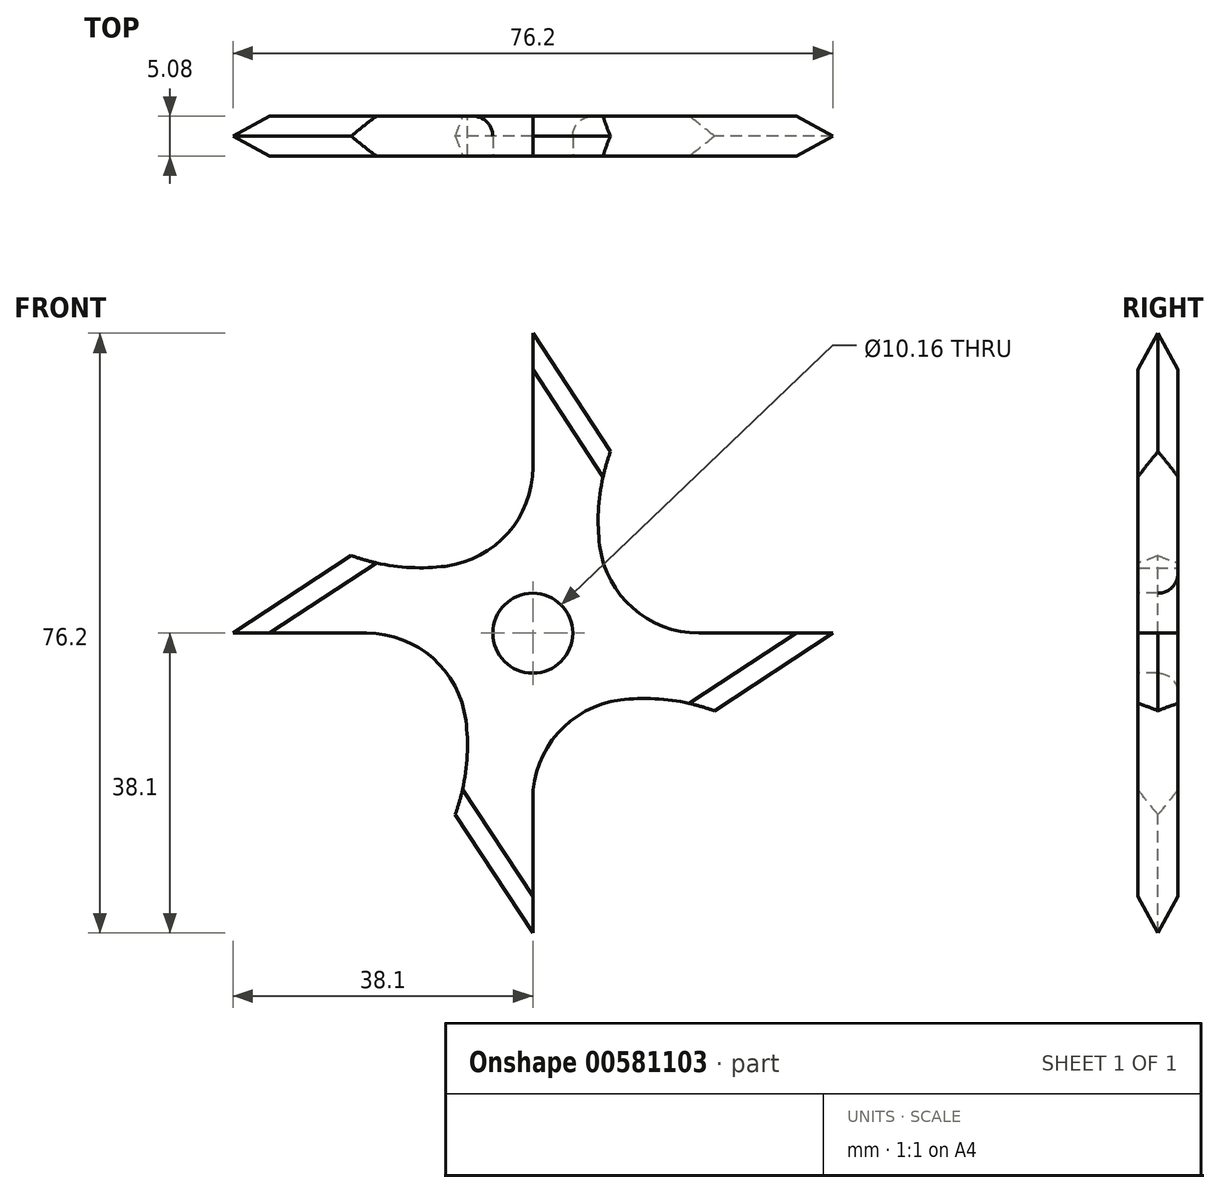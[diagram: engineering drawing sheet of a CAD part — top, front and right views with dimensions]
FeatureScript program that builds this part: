
annotation { "Feature Type Name" : "Feature", "Feature Type Description" : "" }
export const myFeature = defineFeature(function(context is Context, id is Id, definition is map)
    precondition{}
    {
        {
            var Q0;
            Q0=qCreatedBy(makeId("Front.planeOp"),FACE);
            var sketch = newSketch(context, id + "F0", { "sketchPlane" : qUnion([Q0])});
            skLineSegment(sketch, "E0", {"start": v(0, 0) * mm, "end": v(0, 38.1) * mm});
            skLineSegment(sketch, "E1", {"start": v(0, 0) * mm, "end": v(12.7, 0) * mm});
            skLineSegment(sketch, "E2", {"start": v(9.86, 23.06) * mm, "end": v(0, 38.1) * mm});
            skArc(sketch, "E3", {"start": v(9.86, 23.06) * mm, "mid": v(8.5, 11.19) * mm, "end": v(12.7, 0) * mm});
            skLineSegment(sketch, "E4.1.0", {"start": v(-23.06, 9.86) * mm, "end": v(-38.1, 0) * mm});
            skLineSegment(sketch, "E4.1.1", {"start": v(0, 0) * mm, "end": v(-38.1, 0) * mm});
            skArc(sketch, "E4.1.2", {"start": v(-23.06, 9.86) * mm, "mid": v(-11.19, 8.5) * mm, "end": v(0, 12.7) * mm});
            skLineSegment(sketch, "E4.1.3", {"start": v(0, 0) * mm, "end": v(0, 12.7) * mm});
            skLineSegment(sketch, "E4.2.0", {"start": v(-9.86, -23.06) * mm, "end": v(0, -38.1) * mm});
            skLineSegment(sketch, "E4.2.1", {"start": v(0, 0) * mm, "end": v(0, -38.1) * mm});
            skArc(sketch, "E4.2.2", {"start": v(-9.86, -23.06) * mm, "mid": v(-8.5, -11.19) * mm, "end": v(-12.7, 0) * mm});
            skLineSegment(sketch, "E4.2.3", {"start": v(0, 0) * mm, "end": v(-12.7, 0) * mm});
            skLineSegment(sketch, "E4.3.0", {"start": v(23.06, -9.86) * mm, "end": v(38.1, 0) * mm});
            skLineSegment(sketch, "E4.3.1", {"start": v(0, 0) * mm, "end": v(38.1, 0) * mm});
            skArc(sketch, "E4.3.2", {"start": v(23.06, -9.86) * mm, "mid": v(11.19, -8.5) * mm, "end": v(0, -12.7) * mm});
            skLineSegment(sketch, "E4.3.3", {"start": v(0, 0) * mm, "end": v(0, -12.7) * mm});
            skPoint(sketch, "E4.center", {"position": v(0, 0) * mm});
            skSolve(sketch);
        }
        {
            var Q0;
            Q0 = qSketchRegion(id + "F0", true);
            extrude(context, id + "F1", {"entities" : qUnion([Q0]), "depth" : 5.08 * mm, "offsetDistance" : 25.4 * mm});
        }
        {
            var Q0;
            Q0=makeQuery(id+"F1.opExtrude","CAP_FACE",FACE,{"disambiguationData":[OSD([sQuery(id+"F0.wireOp",EDGE,"E0"),sQuery(id+"F0.wireOp",EDGE,"E2"),sQuery(id+"F0.wireOp",EDGE,"E3"),sQuery(id+"F0.wireOp",EDGE,"E4.1.0"),sQuery(id+"F0.wireOp",EDGE,"E4.1.1"),sQuery(id+"F0.wireOp",EDGE,"E4.1.2"),sQuery(id+"F0.wireOp",EDGE,"E4.2.0"),sQuery(id+"F0.wireOp",EDGE,"E4.2.1"),sQuery(id+"F0.wireOp",EDGE,"E4.2.2"),sQuery(id+"F0.wireOp",EDGE,"E4.3.0"),sQuery(id+"F0.wireOp",EDGE,"E4.3.1"),sQuery(id+"F0.wireOp",EDGE,"E4.3.2")])],"isStart":false});
            var sketch = newSketch(context, id + "F2", { "sketchPlane" : qUnion([Q0])});
            skCircle(sketch, "E5", {"center": v(0, 0) * mm, "radius": 5.08 * mm});
            skSolve(sketch);
        }
        {
            var Q0;
            Q0 = qSketchRegion(id + "F2", true);
            extrude(context, id + "F3", {"entities" : qUnion([Q0]), "operationType" : NewBodyOperationType.REMOVE, "oppositeDirection" : true, "depth" : 25.4 * mm, "offsetDistance" : 25.4 * mm});
        }
        {
            var Q0;
            Q0=makeQuery(id+"F1.opExtrude","SWEPT_EDGE",EDGE,{"disambiguationData":[OSD([sQuery(id+"F0.wireOp",EDGE,"E0"),sQuery(id+"F0.wireOp",EDGE,"E4.1.2"),sQuery(id+"F0.wireOp",EDGE,"E4.1.3")])]});
            var Q1;
            Q1=makeQuery(id+"F1.opExtrude","SWEPT_EDGE",EDGE,{"disambiguationData":[OSD([sQuery(id+"F0.wireOp",EDGE,"E3"),sQuery(id+"F0.wireOp",EDGE,"E4.3.1")])]});
            var Q2;
            Q2=makeQuery(id+"F1.opExtrude","SWEPT_EDGE",EDGE,{"disambiguationData":[OSD([sQuery(id+"F0.wireOp",EDGE,"E4.2.1"),sQuery(id+"F0.wireOp",EDGE,"E4.3.2"),sQuery(id+"F0.wireOp",EDGE,"E4.3.3")])]});
            var Q3;
            Q3=makeQuery(id+"F1.opExtrude","SWEPT_EDGE",EDGE,{"disambiguationData":[OSD([sQuery(id+"F0.wireOp",EDGE,"E4.1.1"),sQuery(id+"F0.wireOp",EDGE,"E4.2.2"),sQuery(id+"F0.wireOp",EDGE,"E4.2.3")])]});
            fillet(context, id + "F4", {"entities" : qUnion([Q0, Q1, Q2, Q3]), "radius" : 12.7 * mm, "tangentPropagation" : true, "allowEdgeOverflow" : false});
        }
        {
            var Q0;
            Q0=makeQuery(id+"F1.opExtrude","CAP_EDGE",EDGE,{"disambiguationData":[OSD([sQuery(id+"F0.wireOp",EDGE,"E4.3.0")])],"isStart":true});
            var Q1;
            Q1=makeQuery(id+"F1.opExtrude","CAP_EDGE",EDGE,{"disambiguationData":[OSD([sQuery(id+"F0.wireOp",EDGE,"E4.3.0")])],"isStart":false});
            var Q2;
            Q2=makeQuery(id+"F1.opExtrude","CAP_EDGE",EDGE,{"disambiguationData":[OSD([sQuery(id+"F0.wireOp",EDGE,"E2")])],"isStart":true});
            var Q3;
            Q3=makeQuery(id+"F1.opExtrude","CAP_EDGE",EDGE,{"disambiguationData":[OSD([sQuery(id+"F0.wireOp",EDGE,"E2")])],"isStart":false});
            var Q4;
            Q4=makeQuery(id+"F1.opExtrude","CAP_EDGE",EDGE,{"disambiguationData":[OSD([sQuery(id+"F0.wireOp",EDGE,"E4.2.0")])],"isStart":true});
            var Q5;
            Q5=makeQuery(id+"F1.opExtrude","CAP_EDGE",EDGE,{"disambiguationData":[OSD([sQuery(id+"F0.wireOp",EDGE,"E4.2.0")])],"isStart":false});
            var Q6;
            Q6=makeQuery(id+"F1.opExtrude","CAP_EDGE",EDGE,{"disambiguationData":[OSD([sQuery(id+"F0.wireOp",EDGE,"E4.1.0")])],"isStart":true});
            var Q7;
            Q7=makeQuery(id+"F1.opExtrude","CAP_EDGE",EDGE,{"disambiguationData":[OSD([sQuery(id+"F0.wireOp",EDGE,"E4.1.0")])],"isStart":false});
            chamfer(context, id + "F5", {"entities" : qUnion([Q0, Q1, Q2, Q3, Q4, Q5, Q6, Q7]), "width" : 2.54 * mm, "tangentPropagation" : true});
        }
        {
            var Q0;
            Q0=makeQuery(id+"F3.boolean.opBoolean","INTERSECT",EDGE,{"derivedFrom":[makeQuery(id+"F1.opExtrude","CAP_FACE",FACE,{"disambiguationData":[OSD([sQuery(id+"F0.wireOp",EDGE,"E0"),sQuery(id+"F0.wireOp",EDGE,"E2"),sQuery(id+"F0.wireOp",EDGE,"E3"),sQuery(id+"F0.wireOp",EDGE,"E4.1.0"),sQuery(id+"F0.wireOp",EDGE,"E4.1.1"),sQuery(id+"F0.wireOp",EDGE,"E4.1.2"),sQuery(id+"F0.wireOp",EDGE,"E4.2.0"),sQuery(id+"F0.wireOp",EDGE,"E4.2.1"),sQuery(id+"F0.wireOp",EDGE,"E4.2.2"),sQuery(id+"F0.wireOp",EDGE,"E4.3.0"),sQuery(id+"F0.wireOp",EDGE,"E4.3.1"),sQuery(id+"F0.wireOp",EDGE,"E4.3.2")])],"isStart":true}),makeQuery(id+"F3.opExtrude","SWEPT_FACE",FACE,{"disambiguationData":[OSD([sQuery(id+"F2.wireOp",EDGE,"E5")])]})]});
            var Q1;
            Q1=makeQuery(id+"F3.boolean.opBoolean","COPY",EDGE,{"derivedFrom":makeQuery(id+"F3.opExtrude","CAP_EDGE",EDGE,{"disambiguationData":[OSD([sQuery(id+"F2.wireOp",EDGE,"E5")])],"isStart":true})});
            fillet(context, id + "F6", {"entities" : qUnion([Q0, Q1]), "radius" : 2.54 * mm, "tangentPropagation" : true, "allowEdgeOverflow" : false});
        }
    });
